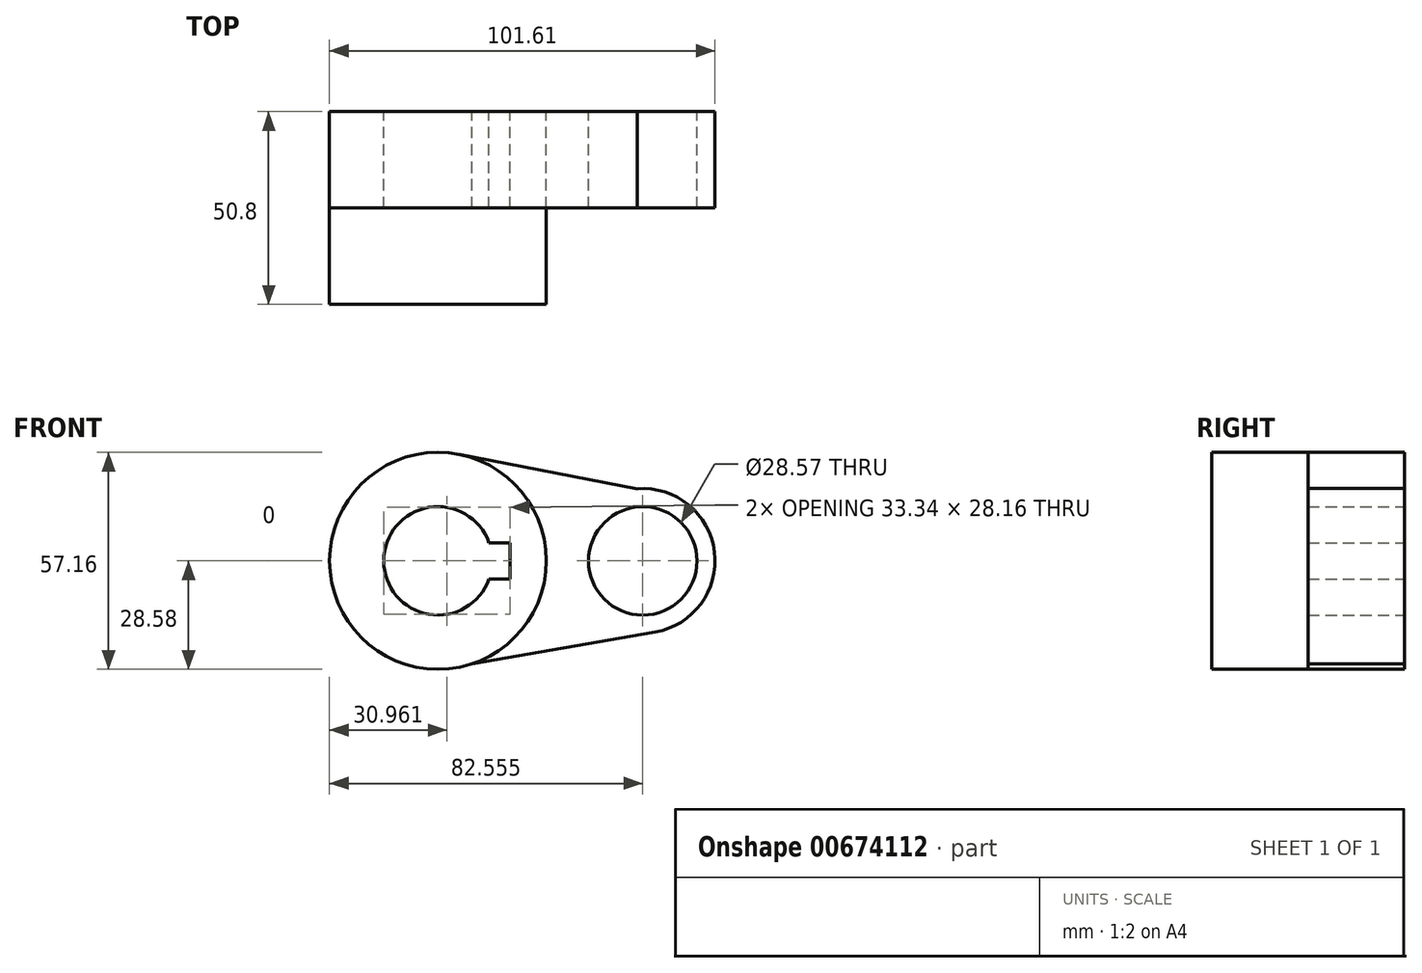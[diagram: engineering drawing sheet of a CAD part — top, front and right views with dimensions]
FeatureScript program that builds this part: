
annotation { "Feature Type Name" : "Feature", "Feature Type Description" : "" }
export const myFeature = defineFeature(function(context is Context, id is Id, definition is map)
    precondition{}
    {
        {
            var Q0;
            Q0=qCreatedBy(makeId("Front.planeOp"),FACE);
            var sketch = newSketch(context, id + "F0", { "sketchPlane" : qUnion([Q0])});
            skCircle(sketch, "E0", {"center": v(0, 0) * mm, "radius": 28.57 * mm});
            skCircle(sketch, "E1", {"center": v(53.98, 0) * mm, "radius": 19.05 * mm});
            skLineSegment(sketch, "E2", {"start": v(5.4, 28.06) * mm, "end": v(52.5, 19) * mm});
            skLineSegment(sketch, "E3", {"start": v(8.94, -27.14) * mm, "end": v(57.23, -18.77) * mm});
            skCircle(sketch, "E4", {"center": v(0, 0) * mm, "radius": 14.29 * mm});
            skCircle(sketch, "E5", {"center": v(53.98, 0) * mm, "radius": 14.29 * mm});
            skLineSegment(sketch, "E6.bottom", {"start": v(19.05, -4.76) * mm, "end": v(-19.05, -4.76) * mm});
            skLineSegment(sketch, "E6.top", {"start": v(19.05, 4.76) * mm, "end": v(-19.05, 4.76) * mm});
            skLineSegment(sketch, "E6.left", {"start": v(19.05, -4.76) * mm, "end": v(19.05, 4.76) * mm});
            skLineSegment(sketch, "E6.right", {"start": v(-19.05, -4.76) * mm, "end": v(-19.05, 4.76) * mm});
            skSolve(sketch);
        }
        {
            var Q0;
            {var subQ0=sQuery(id+"F0.wireOp",EDGE,"E2");Q0=makeQuery(id+"F0.imprint","IMPRINT",FACE,{"disambiguationData":[TD([[makeQuery(id+"F0.imprint","IMPRINT",EDGE,{"derivedFrom":subQ0}),-1.0]])]});}
            var Q1;
            Q1=makeQuery(id+"F0.imprint","IMPRINT",FACE,{"disambiguationData":[TD([[makeQuery(id+"F0.imprint","IMPRINT",EDGE,{"derivedFrom":sQuery(id+"F0.wireOp",EDGE,"E5")}),-1.0]])]});
            var Q2;
            {var subQ5=sQuery(id+"F0.wireOp",EDGE,"E6.right");Q2=makeQuery(id+"F0.imprint","IMPRINT",FACE,{"disambiguationData":[TD([[makeQuery(id+"F0.imprint","IMPRINT",EDGE,{"derivedFrom":subQ5}),-1.0]])]});}
            var Q3;
            {var subQ7=sQuery(id+"F0.wireOp",EDGE,"E6.left");Q3=makeQuery(id+"F0.imprint","IMPRINT",FACE,{"disambiguationData":[TD([[makeQuery(id+"F0.imprint","IMPRINT",EDGE,{"derivedFrom":subQ7}),-1.0]])]});}
            extrude(context, id + "F1", {"entities" : qUnion([Q0, Q1, Q2, Q3]), "depth" : 25.4 * mm, "offsetDistance" : 25.4 * mm});
        }
        {
            var Q0;
            {var subQ7=sQuery(id+"F0.wireOp",EDGE,"E6.left");Q0=makeQuery(id+"F0.imprint","IMPRINT",FACE,{"disambiguationData":[TD([[makeQuery(id+"F0.imprint","IMPRINT",EDGE,{"derivedFrom":subQ7}),-1.0]])]});}
            var Q1;
            {var subQ5=sQuery(id+"F0.wireOp",EDGE,"E6.right");Q1=makeQuery(id+"F0.imprint","IMPRINT",FACE,{"disambiguationData":[TD([[makeQuery(id+"F0.imprint","IMPRINT",EDGE,{"derivedFrom":subQ5}),-1.0]])]});}
            extrude(context, id + "F2", {"entities" : qUnion([Q0, Q1]), "depth" : 50.8 * mm, "offsetDistance" : 25.4 * mm});
        }
    });
